# Revit family: ADB
name_source: partatom
category: Mechanical Equipment
units: mm (PartAtom-declared; Revit-internal decimal feet)

## family parameters
Always vertical = Yes
Cut with Voids When Loaded = No
Part Type = Normal
Room Calculation Point = No
Round Connector Dimension = Use Radius
Shared = No
Work Plane-Based = No

## types (7) — shared parameters
0 = 0' - 0"
1" = 0' - 1"
1.5 = 0' - 1 1/2"
103 = 103.00°
160 = 160.00°
2" = 0' - 2"
2' = 2' - 0"
3" = 0' - 3"
4" = 0' - 4"
60 = 30.00°
Manufacturer = Loren Cook Company
Model = ADB
ONE EIGTH = 0' - 0 1/8"
Type Comments = Tube Axial Drum Fan Cast Aluminum Propeller Belt Drive
URL = www.lorencook.com

## per-type parameters (varying)
| type | (B-C)-1" | (B/2)-C+.125" | -A/2 | A | A/2 | B | B/2 | B/3 | B/6 | C | C/2 |
| 16_ADB | 0' - 8" | 0' - 8 3/8" | -0' - 10" | 1' - 4" | 0' - 8" | 1' - 7 1/2" | 0' - 9 3/4" | 0' - 6 1/2" | 0' - 3 1/4" | 0' - 1 1/2" | 0' - 0 3/4" |
| 20_ADB | 0' - 10" | 0' - 10 3/8" | -0' - 11" | 1' - 6" | 0' - 9" | 1' - 11 1/2" | 0' - 11 3/4" | 0' - 7 27/32" | 0' - 3 29/32" | 0' - 1 1/2" | 0' - 0 3/4" |
| 24_ADB | 1' - 0" | 1' - 0 3/8" | -1' - 0 1/2" | 1' - 9" | 0' - 10 1/2" | 2' - 3 1/2" | 1' - 1 3/4" | 0' - 9 5/32" | 0' - 4 19/32" | 0' - 1 1/2" | 0' - 0 3/4" |
| 30_ADB | 1' - 3" | 1' - 3 3/8" | -1' - 1 1/2" | 1' - 11" | 0' - 11 1/2" | 2' - 9 1/2" | 1' - 4 3/4" | 0' - 11 5/32" | 0' - 5 19/32" | 0' - 1 1/2" | 0' - 0 3/4" |
| 36_ADB | 1' - 6" | 1' - 6 3/8" | -1' - 3" | 2' - 2" | 1' - 1" | 3' - 3 1/2" | 1' - 7 3/4" | 1' - 1 5/32" | 0' - 6 19/32" | 0' - 1 1/2" | 0' - 0 3/4" |
| 42_ADB | 1' - 9 1/16" | 1' - 9 3/8" | -1' - 5" | 2' - 6" | 1' - 3" | 3' - 9 3/4" | 1' - 10 7/8" | 1' - 3 1/4" | 0' - 7 5/8" | 0' - 1 5/8" | 0' - 0 13/16" |
| 48_ADB | 2' - 0 5/16" | 2' - 0 3/8" | -1' - 6" | 2' - 8" | 1' - 4" | 4' - 4 3/4" | 2' - 2 3/8" | 1' - 5 19/32" | 0' - 8 25/32" | 0' - 2 1/8" | 0' - 1 1/16" |

## geometry (parser evidence)
native form markers: Sweep x2
no freeform markers — native parametric forms only
